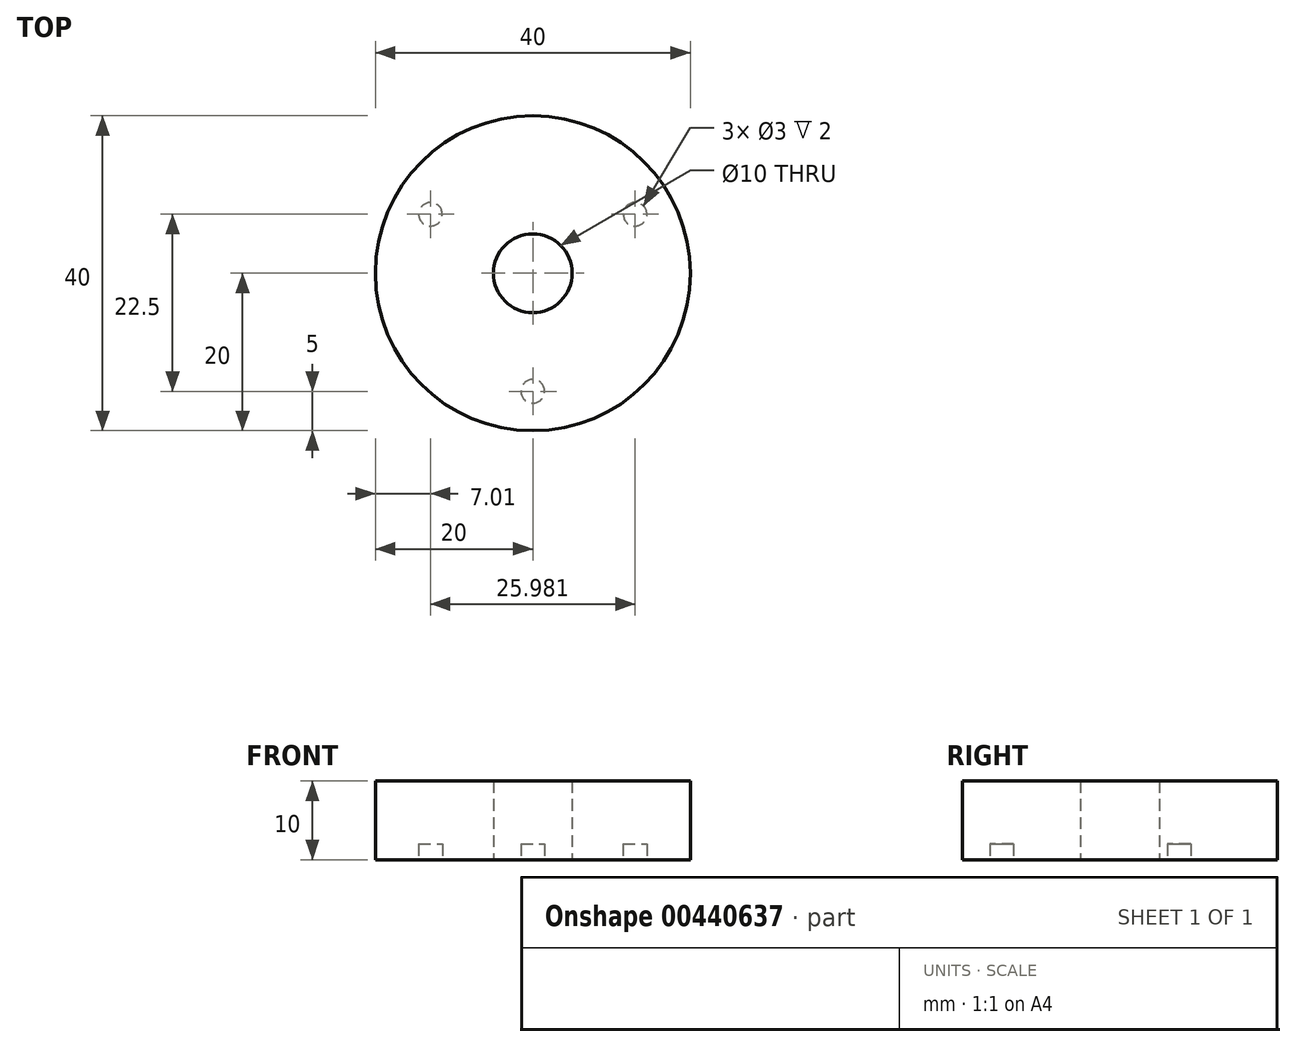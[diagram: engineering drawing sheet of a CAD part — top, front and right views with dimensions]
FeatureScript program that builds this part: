
annotation { "Feature Type Name" : "Feature", "Feature Type Description" : "" }
export const myFeature = defineFeature(function(context is Context, id is Id, definition is map)
    precondition{}
    {
        {
            var Q0;
            Q0=qCreatedBy(makeId("Top.planeOp"),FACE);
            var sketch = newSketch(context, id + "F0", { "sketchPlane" : qUnion([Q0])});
            skCircle(sketch, "E0", {"center": v(0, 0) * mm, "radius": 20 * mm});
            skCircle(sketch, "E1", {"center": v(0, 0) * mm, "radius": 5 * mm});
            skSolve(sketch);
        }
        {
            var Q0;
            Q0 = qSketchRegion(id + "F0", true);
            extrude(context, id + "F1", {"entities" : qUnion([Q0]), "depth" : 10 * mm});
        }
        {
            var Q0;
            Q0=makeQuery(id+"F1.opExtrude","CAP_FACE",FACE,{"disambiguationData":[OSD([sQuery(id+"F0.wireOp",EDGE,"E0"),sQuery(id+"F0.wireOp",EDGE,"E1")])],"isStart":true});
            var sketch = newSketch(context, id + "F2", { "sketchPlane" : qUnion([Q0])});
            skCircle(sketch, "E2", {"center": v(0, 15) * mm, "radius": 1.5 * mm});
            skCircle(sketch, "E3.1.0", {"center": v(-13, -7.5) * mm, "radius": 1.5 * mm});
            skCircle(sketch, "E3.2.0", {"center": v(13, -7.5) * mm, "radius": 1.5 * mm});
            skPoint(sketch, "E3.center", {"position": v(0, 0) * mm});
            skSolve(sketch);
        }
        {
            var Q0;
            Q0 = qSketchRegion(id + "F2", true);
            extrude(context, id + "F3", {"entities" : qUnion([Q0]), "operationType" : NewBodyOperationType.REMOVE, "oppositeDirection" : true, "depth" : 2 * mm});
        }
    });
